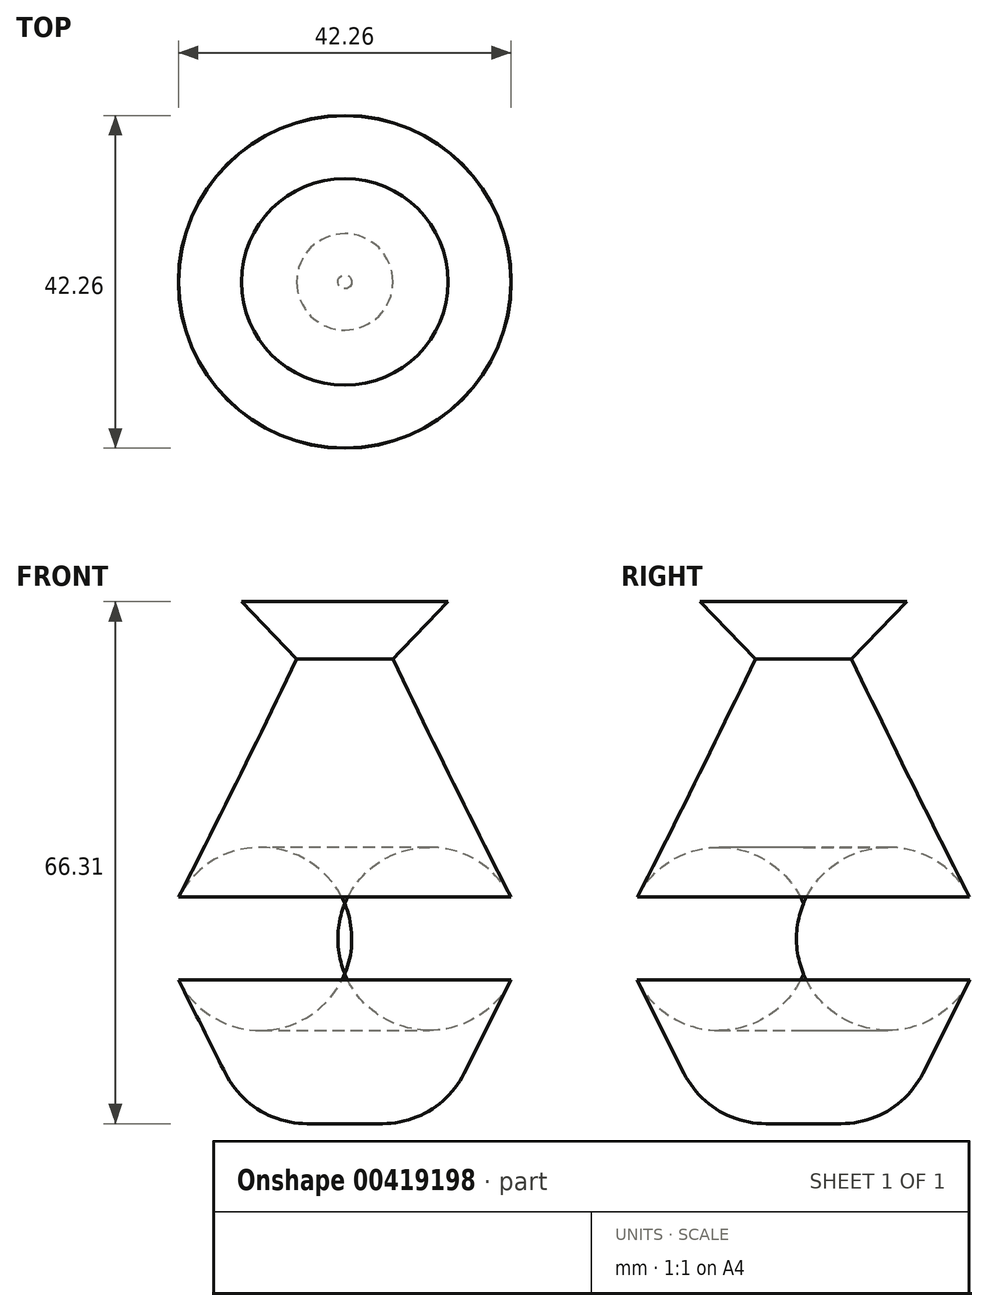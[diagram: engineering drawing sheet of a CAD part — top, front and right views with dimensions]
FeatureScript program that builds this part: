
annotation { "Feature Type Name" : "Feature", "Feature Type Description" : "" }
export const myFeature = defineFeature(function(context is Context, id is Id, definition is map)
    precondition{}
    {
        {
            var Q0;
            Q0=qCreatedBy(makeId("Front.planeOp"),FACE);
            var sketch = newSketch(context, id + "F0", { "sketchPlane" : qUnion([Q0])});
            skLineSegment(sketch, "E0", {"start": v(0, 0) * mm, "end": v(11.95, 0) * mm});
            skLineSegment(sketch, "E1", {"start": v(11.95, 0) * mm, "end": v(24.2, 24.34) * mm});
            skLineSegment(sketch, "E2", {"start": v(24.2, 24.34) * mm, "end": v(6.12, 51.15) * mm});
            skLineSegment(sketch, "E3", {"start": v(6.12, 51.15) * mm, "end": v(6.12, 59.02) * mm});
            skLineSegment(sketch, "E4", {"start": v(6.12, 59.02) * mm, "end": v(13.12, 66.31) * mm});
            skLineSegment(sketch, "E5", {"start": v(13.12, 66.31) * mm, "end": v(0, 66.31) * mm});
            skLineSegment(sketch, "E6", {"start": v(0, 66.31) * mm, "end": v(0, 0) * mm});
            skSolve(sketch);
        }
        {
            var Q0;
            Q0=makeQuery(id+"F0.imprint","IMPRINT",FACE,{"disambiguationData":[TD([[makeQuery(id+"F0.imprint","IMPRINT",EDGE,{"derivedFrom":sQuery(id+"F0.wireOp",EDGE,"E0")}),1.0]])]});
            var Q1;
            Q1=sQuery(id+"F0.wireOp",EDGE,"E6");
            revolve(context, id + "F1", {"entities" : qUnion([Q0]), "axis" : qUnion([Q1]), "revolveType" : RevolveType.FULL});
        }
        {
            var Q0;
            Q0=makeQuery(id+"F1.opRevolve","SWEPT_FACE",FACE,{"disambiguationData":[OSD([sQuery(id+"F0.wireOp",EDGE,"E1")])]});
            fillet(context, id + "F2", {"entities" : qUnion([Q0]), "radius" : 11.63 * mm, "tangentPropagation" : true, "allowEdgeOverflow" : false});
        }
        {
            var Q0;
            Q0=makeQuery(id+"F1.opRevolve","SWEPT_FACE",FACE,{"disambiguationData":[OSD([sQuery(id+"F0.wireOp",EDGE,"E2")])]});
            fillet(context, id + "F3", {"entities" : qUnion([Q0]), "radius" : 1241.43 * mm, "tangentPropagation" : true, "allowEdgeOverflow" : false});
        }
    });
